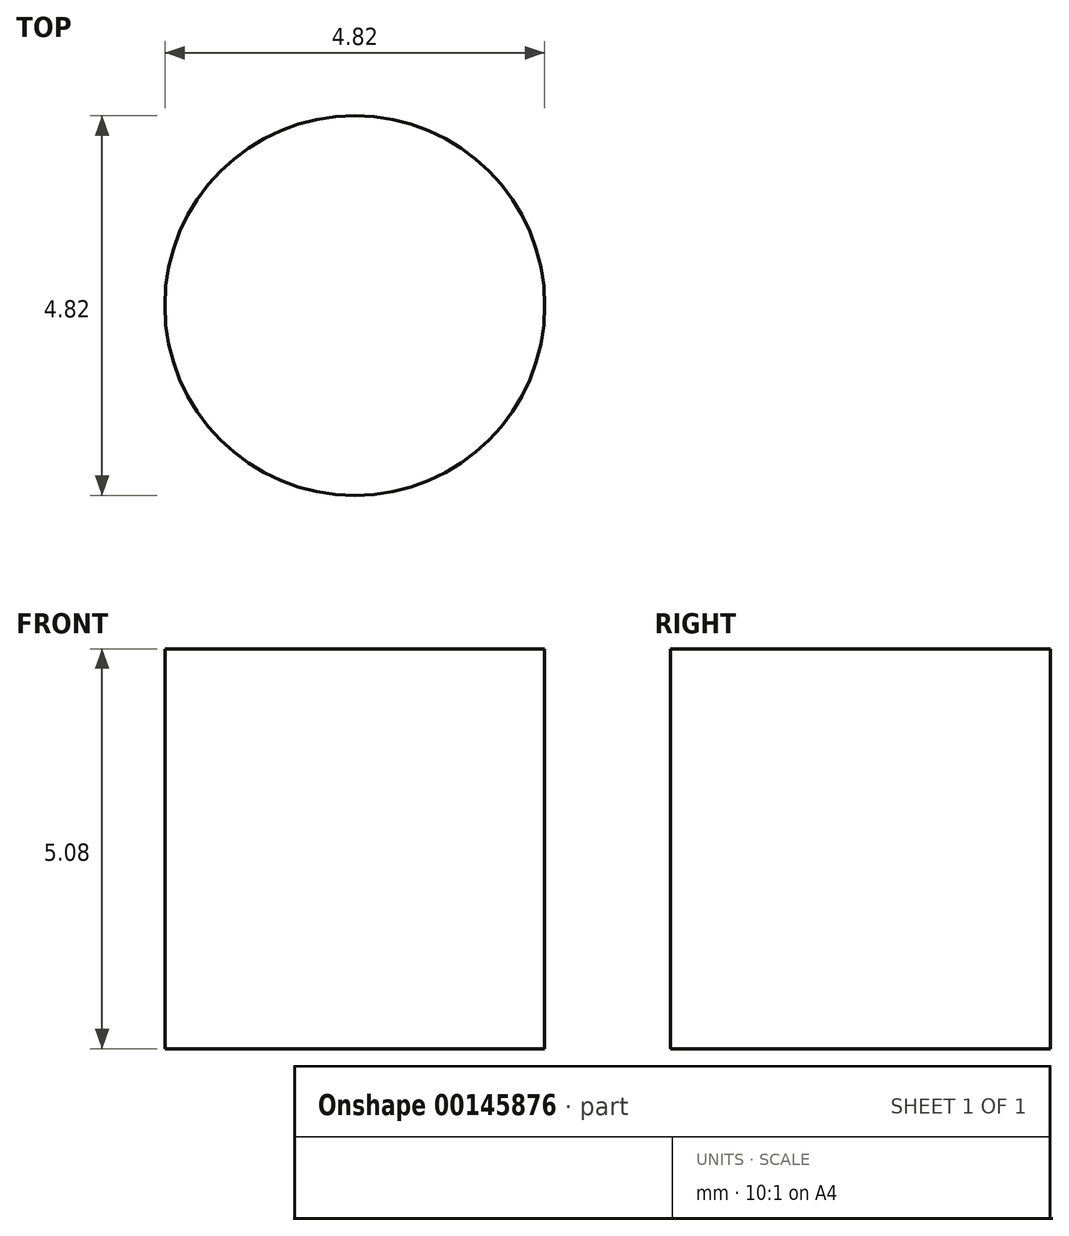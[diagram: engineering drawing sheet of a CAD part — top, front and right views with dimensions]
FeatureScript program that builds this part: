
annotation { "Feature Type Name" : "Feature", "Feature Type Description" : "" }
export const myFeature = defineFeature(function(context is Context, id is Id, definition is map)
    precondition{}
    {
        {
            var Q0;
            Q0=qCreatedBy(makeId("Top.planeOp"),FACE);
            var sketch = newSketch(context, id + "F0", { "sketchPlane" : qUnion([Q0])});
            skCircle(sketch, "E0", {"center": v(0, 0) * mm, "radius": 2.41 * mm});
            skSolve(sketch);
        }
        {
            var Q0;
            Q0 = qSketchRegion(id + "F0", true);
            extrude(context, id + "F1", {"entities" : qUnion([Q0]), "depth" : 5.08 * mm});
        }
    });
